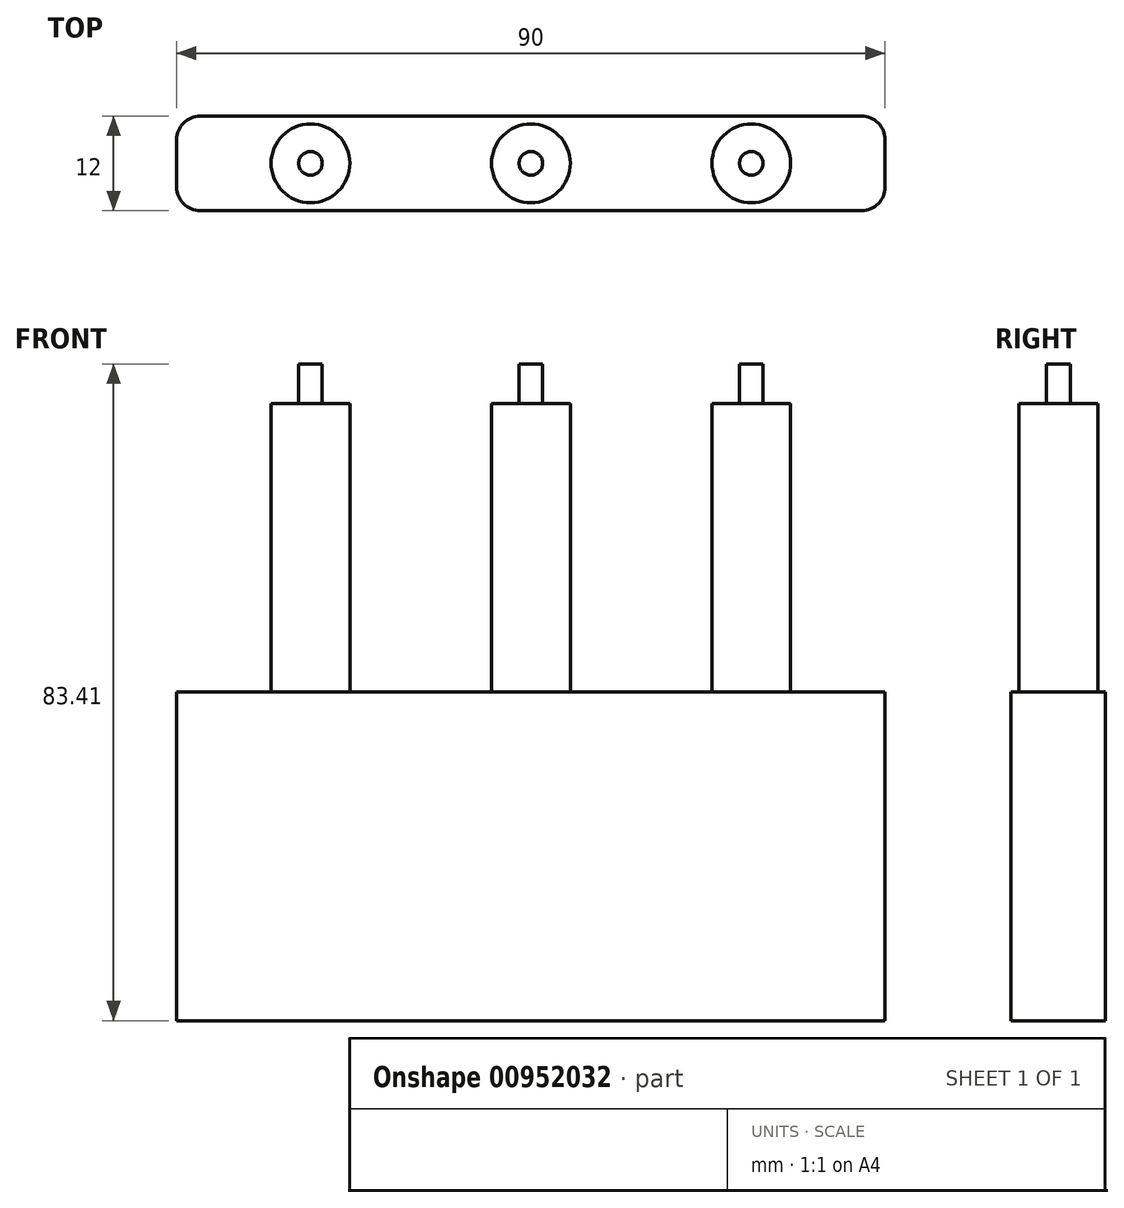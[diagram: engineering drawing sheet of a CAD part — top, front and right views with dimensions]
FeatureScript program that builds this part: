
annotation { "Feature Type Name" : "Feature", "Feature Type Description" : "" }
export const myFeature = defineFeature(function(context is Context, id is Id, definition is map)
    precondition{}
    {
        {
            var Q0;
            Q0=qCreatedBy(makeId("Front.planeOp"),FACE);
            var sketch = newSketch(context, id + "F0", { "sketchPlane" : qUnion([Q0])});
            skLineSegment(sketch, "E0.bottom", {"start": v(-45, 20.89) * mm, "end": v(45, 20.89) * mm});
            skLineSegment(sketch, "E0.top", {"start": v(-45, -20.89) * mm, "end": v(45, -20.89) * mm});
            skLineSegment(sketch, "E0.left", {"start": v(-45, 20.89) * mm, "end": v(-45, -20.89) * mm});
            skLineSegment(sketch, "E0.right", {"start": v(45, 20.89) * mm, "end": v(45, -20.89) * mm});
            skPoint(sketch, "E0.middle", {"position": v(0, 0) * mm});
            skSolve(sketch);
        }
        {
            var Q0;
            Q0=makeQuery(id+"F0.imprint","IMPRINT",FACE,{"disambiguationData":[TD([[makeQuery(id+"F0.imprint","IMPRINT",EDGE,{"derivedFrom":sQuery(id+"F0.wireOp",EDGE,"E0.bottom")}),-1.0]])]});
            extrude(context, id + "F1", {"entities" : qUnion([Q0]), "endBound" : BoundingType.SYMMETRIC, "depth" : 12 * mm, "offsetDistance" : 25 * mm});
        }
        {
            var Q0;
            Q0=makeQuery(id+"F1.opExtrude","SWEPT_FACE",FACE,{"disambiguationData":[OSD([sQuery(id+"F0.wireOp",EDGE,"E0.bottom")])]});
            var sketch = newSketch(context, id + "F2", { "sketchPlane" : qUnion([Q0])});
            skLineSegment(sketch, "E1", {"start": v(0, 0) * mm, "end": v(28, 0) * mm});
            skLineSegment(sketch, "E2", {"start": v(0, 0) * mm, "end": v(-28, 0) * mm});
            skCircle(sketch, "E3", {"center": v(-28, 0) * mm, "radius": 5 * mm});
            skCircle(sketch, "E4", {"center": v(0, 0) * mm, "radius": 5 * mm});
            skCircle(sketch, "E5", {"center": v(28, 0) * mm, "radius": 5 * mm});
            skLineSegment(sketch, "E6", {"start": v(-28, 0) * mm, "end": v(-45, 0) * mm});
            skSolve(sketch);
        }
        {
            var Q0;
            Q0=makeQuery(id+"F2.imprint","IMPRINT",FACE,{"disambiguationData":[TD([[makeQuery(id+"F2.imprint","IMPRINT",EDGE,{"derivedFrom":sQuery(id+"F2.wireOp",EDGE,"E3")}),1.0]])]});
            var Q1;
            {var subQ0=sQuery(id+"F2.wireOp",EDGE,"E2");var subQ1=sQuery(id+"F2.wireOp",EDGE,"E1");var subQ2=makeQuery(id+"F2.imprint","INTERSECT",VERTEX,{"derivedFrom":[subQ1,subQ0]});Q1=makeQuery(id+"F2.imprint","IMPRINT",FACE,{"disambiguationData":[TD([[makeQuery(id+"F2.imprint","IMPRINT",EDGE,{"disambiguationData":[TD([[subQ2,-1.0]])],"derivedFrom":subQ1}),1.0]])]});}
            var Q2;
            {var subQ0=sQuery(id+"F2.wireOp",EDGE,"E2");var subQ1=sQuery(id+"F2.wireOp",EDGE,"E1");var subQ2=makeQuery(id+"F2.imprint","INTERSECT",VERTEX,{"derivedFrom":[subQ1,subQ0]});Q2=makeQuery(id+"F2.imprint","IMPRINT",FACE,{"disambiguationData":[TD([[makeQuery(id+"F2.imprint","IMPRINT",EDGE,{"disambiguationData":[TD([[subQ2,-1.0]])],"derivedFrom":subQ1}),-1.0]])]});}
            var Q3;
            Q3=makeQuery(id+"F2.imprint","IMPRINT",FACE,{"disambiguationData":[TD([[makeQuery(id+"F2.imprint","IMPRINT",EDGE,{"derivedFrom":sQuery(id+"F2.wireOp",EDGE,"E5")}),1.0]])]});
            extrude(context, id + "F3", {"entities" : qUnion([Q0, Q1, Q2, Q3]), "operationType" : NewBodyOperationType.ADD, "depth" : 36.63 * mm, "offsetDistance" : 25 * mm});
        }
        {
            var Q0;
            Q0=makeQuery(id+"F1.opExtrude","CAP_EDGE",EDGE,{"disambiguationData":[OSD([sQuery(id+"F0.wireOp",EDGE,"E0.right")])],"isStart":false});
            var Q1;
            Q1=makeQuery(id+"F1.opExtrude","CAP_EDGE",EDGE,{"disambiguationData":[OSD([sQuery(id+"F0.wireOp",EDGE,"E0.right")])],"isStart":true});
            var Q2;
            Q2=makeQuery(id+"F1.opExtrude","CAP_EDGE",EDGE,{"disambiguationData":[OSD([sQuery(id+"F0.wireOp",EDGE,"E0.left")])],"isStart":false});
            var Q3;
            Q3=makeQuery(id+"F1.opExtrude","CAP_EDGE",EDGE,{"disambiguationData":[OSD([sQuery(id+"F0.wireOp",EDGE,"E0.left")])],"isStart":true});
            var Q4;
            Q4=makeQuery(id+"F2s3ULIVNC9lstZ_1.opExtrude","SWEPT_EDGE",EDGE,{"disambiguationData":[OSD([sQuery(id+"FA5orne9ivkbIlC_1.wireOp",EDGE,"wairj4QB-Xcb8-0EUV-3ZTy-Z43z6KPD097e.bottom"),sQuery(id+"FA5orne9ivkbIlC_1.wireOp",EDGE,"wairj4QB-Xcb8-0EUV-3ZTy-Z43z6KPD097e.left")])]});
            var Q5;
            Q5=makeQuery(id+"F2s3ULIVNC9lstZ_1.opExtrude","SWEPT_EDGE",EDGE,{"disambiguationData":[OSD([sQuery(id+"FA5orne9ivkbIlC_1.wireOp",EDGE,"wairj4QB-Xcb8-0EUV-3ZTy-Z43z6KPD097e.top"),sQuery(id+"FA5orne9ivkbIlC_1.wireOp",EDGE,"wairj4QB-Xcb8-0EUV-3ZTy-Z43z6KPD097e.left")])]});
            var Q6;
            Q6=makeQuery(id+"F2s3ULIVNC9lstZ_1.opExtrude","SWEPT_EDGE",EDGE,{"disambiguationData":[OSD([sQuery(id+"FA5orne9ivkbIlC_1.wireOp",EDGE,"wairj4QB-Xcb8-0EUV-3ZTy-Z43z6KPD097e.top"),sQuery(id+"FA5orne9ivkbIlC_1.wireOp",EDGE,"wairj4QB-Xcb8-0EUV-3ZTy-Z43z6KPD097e.right")])]});
            var Q7;
            Q7=makeQuery(id+"F2s3ULIVNC9lstZ_1.opExtrude","SWEPT_EDGE",EDGE,{"disambiguationData":[OSD([sQuery(id+"FA5orne9ivkbIlC_1.wireOp",EDGE,"wairj4QB-Xcb8-0EUV-3ZTy-Z43z6KPD097e.bottom"),sQuery(id+"FA5orne9ivkbIlC_1.wireOp",EDGE,"wairj4QB-Xcb8-0EUV-3ZTy-Z43z6KPD097e.right")])]});
            fillet(context, id + "F4", {"entities" : qUnion([Q0, Q1, Q2, Q3, Q4, Q5, Q6, Q7]), "radius" : 3 * mm, "tangentPropagation" : true, "allowEdgeOverflow" : false});
        }
        {
            var Q0;
            Q0=makeQuery(id+"F3.opExtrude","CAP_FACE",FACE,{"disambiguationData":[OSD([sQuery(id+"F2.wireOp",EDGE,"E3")])],"isStart":false});
            var sketch = newSketch(context, id + "F5", { "sketchPlane" : qUnion([Q0])});
            skCircle(sketch, "E7", {"center": v(-28, 0) * mm, "radius": 1.5 * mm});
            skCircle(sketch, "E8", {"center": v(0, 0) * mm, "radius": 1.5 * mm});
            skCircle(sketch, "E9.0", {"center": v(28, 0) * mm, "radius": 5 * mm});
            skCircle(sketch, "E10", {"center": v(28, 0) * mm, "radius": 1.5 * mm});
            skSolve(sketch);
        }
        {
            var Q0;
            Q0=makeQuery(id+"F5.imprint","IMPRINT",FACE,{"disambiguationData":[TD([[makeQuery(id+"F5.imprint","IMPRINT",EDGE,{"derivedFrom":sQuery(id+"F5.wireOp",EDGE,"E7")}),1.0]])]});
            var Q1;
            Q1=makeQuery(id+"F5.imprint","IMPRINT",FACE,{"disambiguationData":[TD([[makeQuery(id+"F5.imprint","IMPRINT",EDGE,{"derivedFrom":sQuery(id+"F5.wireOp",EDGE,"E8")}),1.0]])]});
            var Q2;
            Q2=makeQuery(id+"F5.imprint","IMPRINT",FACE,{"disambiguationData":[TD([[makeQuery(id+"F5.imprint","IMPRINT",EDGE,{"derivedFrom":sQuery(id+"F5.wireOp",EDGE,"E10")}),1.0]])]});
            extrude(context, id + "F6", {"entities" : qUnion([Q0, Q1, Q2]), "operationType" : NewBodyOperationType.ADD, "depth" : 5 * mm, "offsetDistance" : 25 * mm});
        }
    });
